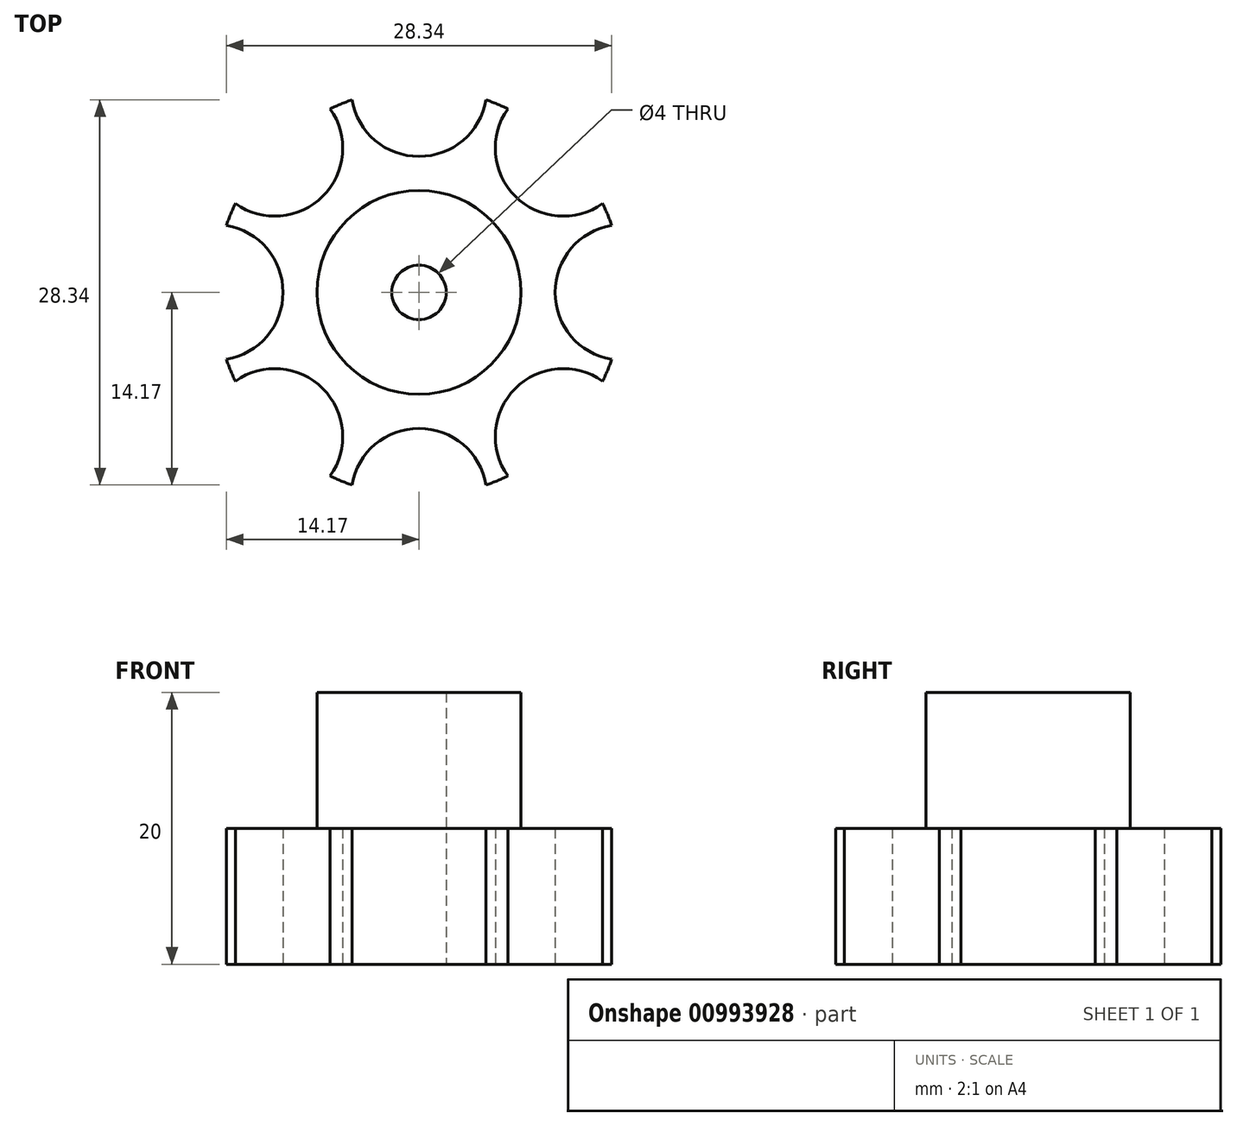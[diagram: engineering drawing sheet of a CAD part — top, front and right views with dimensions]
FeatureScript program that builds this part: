
annotation { "Feature Type Name" : "Feature", "Feature Type Description" : "" }
export const myFeature = defineFeature(function(context is Context, id is Id, definition is map)
    precondition{}
    {
        {
            var Q0;
            Q0=qCreatedBy(makeId("Top.planeOp"),FACE);
            var sketch = newSketch(context, id + "F0", { "sketchPlane" : qUnion([Q0])});
            skArc(sketch, "E0", {"start": v(13.5, -6.53) * mm, "mid": v(13.86, -5.74) * mm, "end": v(14.17, -4.93) * mm});
            skLineSegment(sketch, "E1", {"start": v(0, -15) * mm, "end": v(0, 15) * mm, "construction": true});
            skLineSegment(sketch, "E2", {"start": v(-15, 0) * mm, "end": v(15, 0) * mm, "construction": true});
            skArc(sketch, "E3", {"start": v(-14.17, -4.93) * mm, "mid": v(-10, 0) * mm, "end": v(-14.17, 4.93) * mm});
            skArc(sketch, "E4", {"start": v(4.93, -14.17) * mm, "mid": v(0, -10) * mm, "end": v(-4.93, -14.17) * mm});
            skArc(sketch, "E5", {"start": v(-4.93, 14.17) * mm, "mid": v(0, 10) * mm, "end": v(4.93, 14.17) * mm});
            skArc(sketch, "E6", {"start": v(14.17, 4.93) * mm, "mid": v(10, 0) * mm, "end": v(14.17, -4.93) * mm});
            skLineSegment(sketch, "E7", {"start": v(-10.6, -10.6) * mm, "end": v(10.6, 10.6) * mm, "construction": true});
            skLineSegment(sketch, "E8", {"start": v(10.6, -10.6) * mm, "end": v(-10.6, 10.6) * mm, "construction": true});
            skArc(sketch, "E9", {"start": v(13.5, -6.53) * mm, "mid": v(7.07, -7.07) * mm, "end": v(6.53, -13.5) * mm});
            skArc(sketch, "E10", {"start": v(-6.53, -13.5) * mm, "mid": v(-7.07, -7.07) * mm, "end": v(-13.5, -6.53) * mm});
            skArc(sketch, "E11", {"start": v(-13.5, 6.53) * mm, "mid": v(-7.07, 7.07) * mm, "end": v(-6.53, 13.5) * mm});
            skArc(sketch, "E12", {"start": v(6.53, 13.5) * mm, "mid": v(7.07, 7.07) * mm, "end": v(13.5, 6.53) * mm});
            skArc(sketch, "E13.trimOffspring", {"start": v(14.17, 4.93) * mm, "mid": v(13.86, 5.74) * mm, "end": v(13.5, 6.53) * mm});
            skArc(sketch, "E14.trimOffspring", {"start": v(6.53, 13.5) * mm, "mid": v(5.74, 13.86) * mm, "end": v(4.93, 14.17) * mm});
            skArc(sketch, "E15.trimOffspring", {"start": v(-4.93, 14.17) * mm, "mid": v(-5.74, 13.86) * mm, "end": v(-6.53, 13.5) * mm});
            skArc(sketch, "E16.trimOffspring", {"start": v(-13.5, 6.53) * mm, "mid": v(-13.86, 5.74) * mm, "end": v(-14.17, 4.93) * mm});
            skArc(sketch, "E17.trimOffspring", {"start": v(-14.17, -4.93) * mm, "mid": v(-13.86, -5.74) * mm, "end": v(-13.5, -6.53) * mm});
            skArc(sketch, "E18.trimOffspring", {"start": v(-6.53, -13.5) * mm, "mid": v(-5.74, -13.86) * mm, "end": v(-4.93, -14.17) * mm});
            skArc(sketch, "E19.trimOffspring", {"start": v(4.93, -14.17) * mm, "mid": v(5.74, -13.86) * mm, "end": v(6.53, -13.5) * mm});
            skCircle(sketch, "E20", {"center": v(0, 0) * mm, "radius": 2 * mm});
            skSolve(sketch);
        }
        {
            var Q0;
            Q0 = qSketchRegion(id + "F0", true);
            extrude(context, id + "F1", {"entities" : qUnion([Q0]), "depth" : 10 * mm, "offsetDistance" : 25 * mm});
        }
        {
            var Q0;
            Q0=makeQuery(id+"F1.opExtrude","CAP_FACE",FACE,{"disambiguationData":[OSD([sQuery(id+"F0.wireOp",EDGE,"E0"),sQuery(id+"F0.wireOp",EDGE,"E3"),sQuery(id+"F0.wireOp",EDGE,"E4"),sQuery(id+"F0.wireOp",EDGE,"E5"),sQuery(id+"F0.wireOp",EDGE,"E6"),sQuery(id+"F0.wireOp",EDGE,"E9"),sQuery(id+"F0.wireOp",EDGE,"E10"),sQuery(id+"F0.wireOp",EDGE,"E11"),sQuery(id+"F0.wireOp",EDGE,"E12"),sQuery(id+"F0.wireOp",EDGE,"E13.trimOffspring"),sQuery(id+"F0.wireOp",EDGE,"E14.trimOffspring"),sQuery(id+"F0.wireOp",EDGE,"E15.trimOffspring"),sQuery(id+"F0.wireOp",EDGE,"E16.trimOffspring"),sQuery(id+"F0.wireOp",EDGE,"E17.trimOffspring"),sQuery(id+"F0.wireOp",EDGE,"E18.trimOffspring"),sQuery(id+"F0.wireOp",EDGE,"E19.trimOffspring"),sQuery(id+"F0.wireOp",EDGE,"E20")])],"isStart":false});
            var sketch = newSketch(context, id + "F2", { "sketchPlane" : qUnion([Q0])});
            skCircle(sketch, "E21", {"center": v(0, 0) * mm, "radius": 7.5 * mm});
            skCircle(sketch, "E22", {"center": v(0, 0) * mm, "radius": 2 * mm});
            skSolve(sketch);
        }
        {
            var Q0;
            Q0 = qSketchRegion(id + "F2", true);
            extrude(context, id + "F3", {"entities" : qUnion([Q0]), "operationType" : NewBodyOperationType.ADD, "depth" : 10 * mm, "offsetDistance" : 25 * mm});
        }
    });
